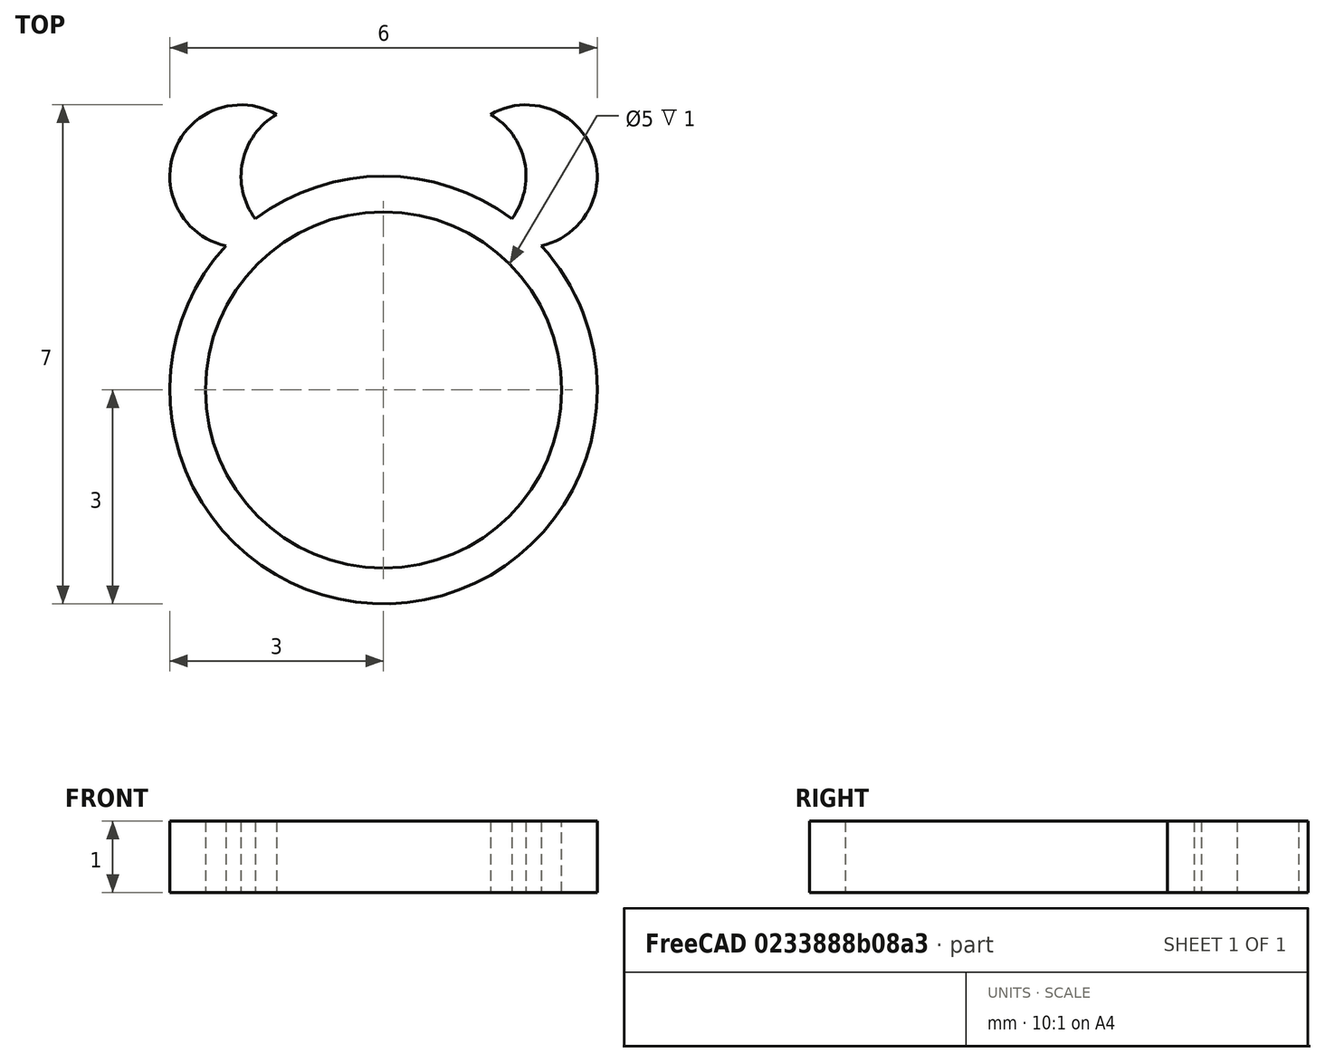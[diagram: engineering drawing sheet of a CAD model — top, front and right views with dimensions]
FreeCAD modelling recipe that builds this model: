
FCSTD DOCUMENT  (FreeCAD 0.19R)
Label: Reto 7
License: All rights reserved
LicenseURL: http://en.wikipedia.org/wiki/All_rights_reserved
objects: App::MeasureDistance×9, Part::Cylinder×6, Part::Cut×3, Part::MultiFuse×1
note: 10 computed .brp shape members not serialized (recipe doc carries the construction recipe); baked Part::Feature solids carry a one-line shape summary decoded from their .brp

FEATURE [Part::Cylinder] Cylinder  label="Cilindro"
  Angle = 360
  AttacherType = Attacher::AttachEngine3D
  Height = 1
  Radius = 3
FEATURE [Part::Cylinder] Cylinder001  label="Cilindro001"
  Angle = 360
  AttacherType = Attacher::AttachEngine3D
  Height = 5
  Placement = pos=(0,0,-2) rot=(0,0,1;0rad)
  Radius = 2.5
FEATURE [Part::Cut] Cut  label="Anillo"
  Base = -> Cylinder
  Refine = true
  Tool = -> Cylinder001
FEATURE [Part::Cylinder] Cylinder002  label="Cilindro002"
  Angle = 360
  AttacherType = Attacher::AttachEngine3D
  Height = 1
  Placement = pos=(-8,0,0) rot=(0,0,1;0rad)
  Radius = 1
FEATURE [Part::Cylinder] Cylinder003  label="Cilindro003"
  Angle = 360
  AttacherType = Attacher::AttachEngine3D
  Height = 1
  Placement = pos=(-7,0,0) rot=(0,0,1;0rad)
  Radius = 1
FEATURE [Part::Cut] Cut001  label="Cuerno 1"
  Base = -> Cylinder002
  Placement = pos=(6,3,0) rot=(0,0,1;0rad)
  Refine = true
  Tool = -> Cylinder003
FEATURE [Part::Cylinder] Cylinder004  label="Cilindro004"
  Angle = 360
  AttacherType = Attacher::AttachEngine3D
  Height = 1
  Placement = pos=(-8,0,0) rot=(0,0,1;0rad)
  Radius = 1
FEATURE [Part::Cylinder] Cylinder005  label="Cilindro005"
  Angle = 360
  AttacherType = Attacher::AttachEngine3D
  Height = 1
  Placement = pos=(-7,0,0) rot=(0,0,1;0rad)
  Radius = 1
FEATURE [Part::Cut] Cut002
  Base = -> Cylinder004
  Placement = pos=(-6,3,0) rot=(0,0,1;3.14159rad)
  Refine = true
  Tool = -> Cylinder005
FEATURE [Part::MultiFuse] Fusion  label="Reto 7"
  Refine = true
  Shapes = -> [Cut,Cut001,Cut002]
FEATURE [App::MeasureDistance] Distance  label="Distance: 1,50 mm"
  Distance = 1.49641
  P1 = (-1.5,3.86603,1)
  P2 = (-1.8,2.4,1)
FEATURE [App::MeasureDistance] Distance001  label="Distance: 1,01 mm"
  Distance = 1.00749
  P1 = (-2.99235,3.12347,1)
  P2 = (-1.99325,2.9937,1)
FEATURE [App::MeasureDistance] Distance002  label="Distance: 5,98 mm"
  Distance = 5.97688
  P1 = (0.0361841,2.99708,1)
  P2 = (0.324044,-2.97286,1)
FEATURE [App::MeasureDistance] Distance003  label="Distance: 4,91 mm"
  Distance = 4.90917
  P1 = (-0.573864,2.42165,1)
  P2 = (1.34615,-2.09648,1)
FEATURE [App::MeasureDistance] Distance004  label="Distance: 4,21 mm"
  Distance = 4.21335
  P1 = (2.07824,3.04835,1)
  P2 = (-2.01279,3.07527,2.00749)
FEATURE [App::MeasureDistance] Distance005  label="Distance: 0,56 mm"
  Distance = 0.560378
  P1 = (2.21494,2.02337,1)
  P2 = (1.8,2.4,1)
FEATURE [App::MeasureDistance] Distance006  label="Distance: 1,00 mm"
  Distance = 1.00326
  P1 = (-0.252574,-2.98268,1)
  P2 = (-0.17183,-2.98531,0)
FEATURE [App::MeasureDistance] Distance007  label="Distance: 1,96 mm"
  Distance = 1.96108
  P1 = (-2.06802,3.99037,0.358414)
  P2 = (-2.2593,2.03905,0.318042)
FEATURE [App::MeasureDistance] Distance008  label="Distance: 5,41 mm"
  Distance = 5.40876
  P1 = (-2.29736,2.05251,0.492988)
  P2 = (-0.31832,-2.98054,0.412244)
